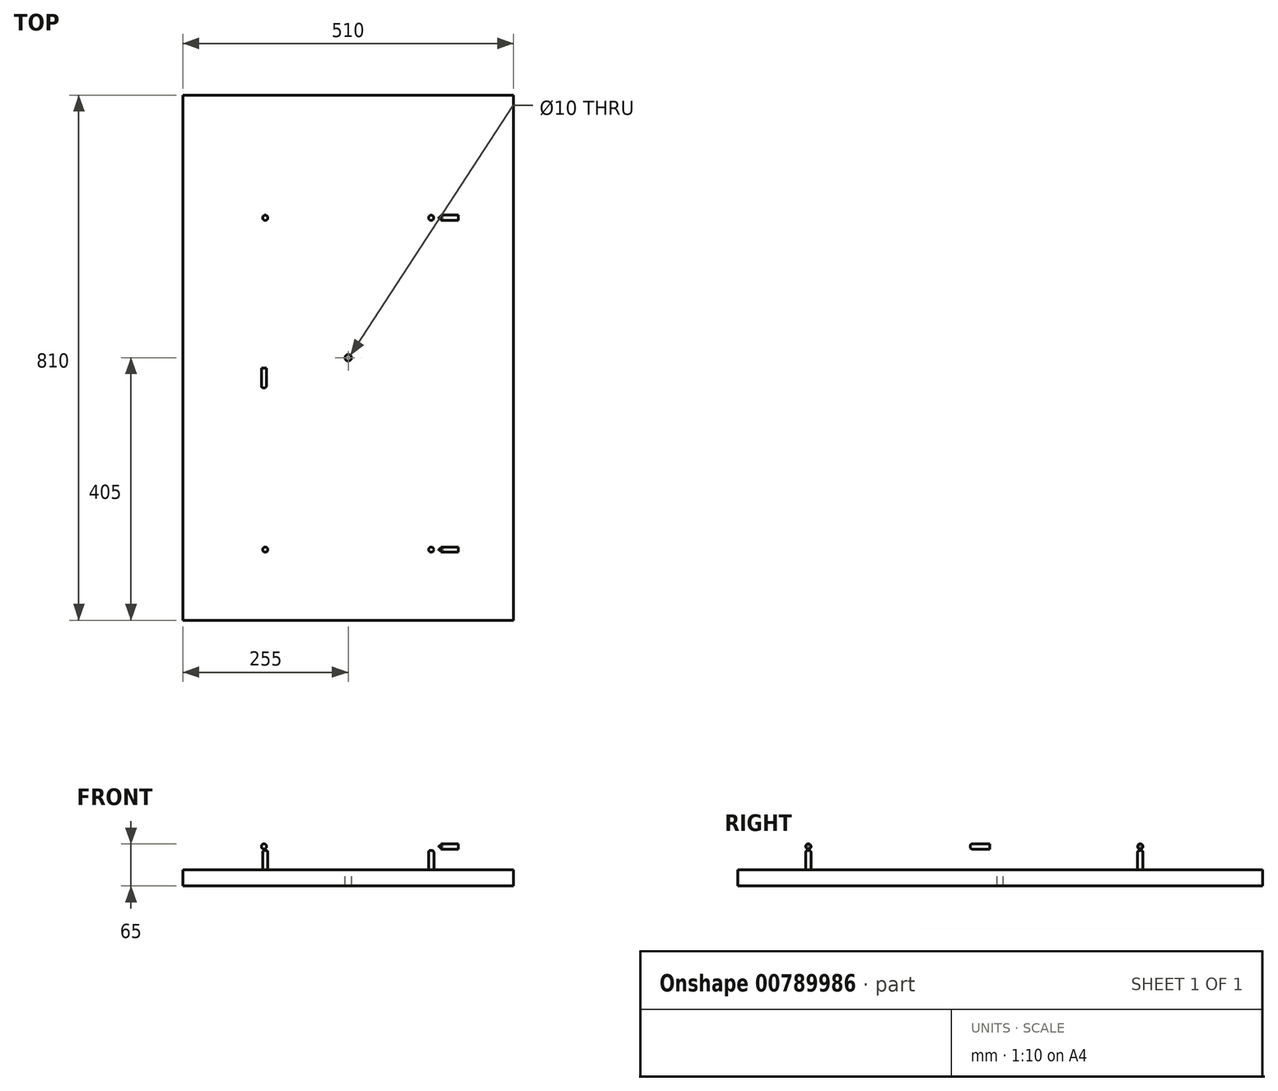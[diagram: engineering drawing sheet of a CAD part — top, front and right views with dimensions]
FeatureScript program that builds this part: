
annotation { "Feature Type Name" : "Feature", "Feature Type Description" : "" }
export const myFeature = defineFeature(function(context is Context, id is Id, definition is map)
    precondition{}
    {
        {
            var Q0;
            Q0=qCreatedBy(makeId("Right.planeOp"),FACE);
            var sketch = newSketch(context, id + "F0", { "sketchPlane" : qUnion([Q0])});
            skLineSegment(sketch, "E0.bottom", {"start": v(0, 0) * mm, "end": v(-810, 0) * mm});
            skLineSegment(sketch, "E0.top", {"start": v(0, 25) * mm, "end": v(-810, 25) * mm});
            skLineSegment(sketch, "E0.left", {"start": v(0, 0) * mm, "end": v(0, 25) * mm});
            skLineSegment(sketch, "E0.right", {"start": v(-810, 0) * mm, "end": v(-810, 25) * mm});
            skSolve(sketch);
        }
        {
            var Q0;
            Q0=makeQuery(id+"F0.imprint","IMPRINT",FACE,{"disambiguationData":[TD([[makeQuery(id+"F0.imprint","IMPRINT",EDGE,{"derivedFrom":sQuery(id+"F0.wireOp",EDGE,"E0.bottom")}),-1.0]])]});
            extrude(context, id + "F1", {"entities" : qUnion([Q0]), "depth" : 510 * mm, "offsetDistance" : 25 * mm});
        }
        {
            var Q0;
            Q0=makeQuery(id+"F1.opExtrude","SWEPT_FACE",FACE,{"disambiguationData":[OSD([sQuery(id+"F0.wireOp",EDGE,"E0.top")])]});
            var sketch = newSketch(context, id + "F2", { "sketchPlane" : qUnion([Q0])});
            skPoint(sketch, "E1", {"position": v(255, -405) * mm});
            skSolve(sketch);
        }
        {
            var Q0;
            Q0=sQuery(id+"F2.wireOp",VERTEX,"E1");
            var Q1;
            Q1=makeQuery(id+"F1.opExtrude","SWEPT_BODY",BODY,{"disambiguationData":[OSD([sQuery(id+"F0.wireOp",EDGE,"E0.bottom"),sQuery(id+"F0.wireOp",EDGE,"E0.top"),sQuery(id+"F0.wireOp",EDGE,"E0.left"),sQuery(id+"F0.wireOp",EDGE,"E0.right")])]});
            hole(context, id + "F3", {"style" : HoleStyle.SIMPLE, "endStyle" : HoleEndStyle.THROUGH, "holeDiameter" : 10 * mm, "majorDiameter" : 5 * mm, "isTappedThrough" : true, "tappedDepth" : 12 * mm, "tapClearance" : 3, "locations" : qUnion([Q0]), "scope" : qUnion([Q1])});
        }
        {
            var Q0;
            Q0=makeQuery(id+"F1.opExtrude","SWEPT_FACE",FACE,{"disambiguationData":[OSD([sQuery(id+"F0.wireOp",EDGE,"E0.top")])]});
            var sketch = newSketch(context, id + "F4", { "sketchPlane" : qUnion([Q0])});
            skLineSegment(sketch, "E2", {"start": v(255, -405) * mm, "end": v(127, -405) * mm});
            skLineSegment(sketch, "E3", {"start": v(127, -405) * mm, "end": v(127, -189) * mm});
            skCircle(sketch, "E4", {"center": v(127, -189) * mm, "radius": 4 * mm});
            skLineSegment(sketch, "E5", {"start": v(255, -405) * mm, "end": v(383, -405) * mm});
            skLineSegment(sketch, "E6", {"start": v(383, -405) * mm, "end": v(383, -189) * mm});
            skCircle(sketch, "E7", {"center": v(383, -189) * mm, "radius": 4 * mm});
            skLineSegment(sketch, "E8", {"start": v(127, -405) * mm, "end": v(127, -701) * mm});
            skLineSegment(sketch, "E9", {"start": v(383, -405) * mm, "end": v(383, -701) * mm});
            skCircle(sketch, "E10", {"center": v(127, -701) * mm, "radius": 4 * mm});
            skCircle(sketch, "E11", {"center": v(383, -701) * mm, "radius": 4 * mm});
            skSolve(sketch);
        }
        {
            var Q0;
            Q0=makeQuery(id+"F4.imprint","IMPRINT",FACE,{"disambiguationData":[TD([[makeQuery(id+"F4.imprint","IMPRINT",EDGE,{"derivedFrom":sQuery(id+"F4.wireOp",EDGE,"E10")}),1.0]])]});
            var Q1;
            Q1=makeQuery(id+"F4.imprint","IMPRINT",FACE,{"disambiguationData":[TD([[makeQuery(id+"F4.imprint","IMPRINT",EDGE,{"derivedFrom":sQuery(id+"F4.wireOp",EDGE,"E11")}),1.0]])]});
            var Q2;
            Q2=makeQuery(id+"F4.imprint","IMPRINT",FACE,{"disambiguationData":[TD([[makeQuery(id+"F4.imprint","IMPRINT",EDGE,{"derivedFrom":sQuery(id+"F4.wireOp",EDGE,"E7")}),1.0]])]});
            var Q3;
            Q3=makeQuery(id+"F4.imprint","IMPRINT",FACE,{"disambiguationData":[TD([[makeQuery(id+"F4.imprint","IMPRINT",EDGE,{"derivedFrom":sQuery(id+"F4.wireOp",EDGE,"E4")}),1.0]])]});
            extrude(context, id + "F5", {"entities" : qUnion([Q0, Q1, Q2, Q3]), "operationType" : NewBodyOperationType.ADD, "depth" : 30 * mm, "offsetDistance" : 25 * mm});
        }
        {
            var Q0;
            Q0=makeQuery(id+"F5.opExtrude","CAP_EDGE",EDGE,{"disambiguationData":[OSD([sQuery(id+"F4.wireOp",EDGE,"E10")])],"isStart":false});
            var Q1;
            Q1=makeQuery(id+"F5.opExtrude","CAP_FACE",FACE,{"disambiguationData":[OSD([sQuery(id+"F4.wireOp",EDGE,"E11")])],"isStart":false});
            var Q2;
            Q2=makeQuery(id+"F5.opExtrude","CAP_EDGE",EDGE,{"disambiguationData":[OSD([sQuery(id+"F4.wireOp",EDGE,"E7")])],"isStart":false});
            var Q3;
            Q3=makeQuery(id+"F5.opExtrude","CAP_EDGE",EDGE,{"disambiguationData":[OSD([sQuery(id+"F4.wireOp",EDGE,"E4")])],"isStart":false});
            fillet(context, id + "F6", {"entities" : qUnion([Q0, Q1, Q2, Q3]), "radius" : 3 * mm, "tangentPropagation" : true, "allowEdgeOverflow" : false});
        }
        {
            var Q0;
            Q0=qCreatedBy(makeId("Right.planeOp"),FACE);
            cPlane(context, id + "F7", {"entities" : qUnion([Q0]), "cplaneType" : CPlaneType.OFFSET, "offset" : 395 * mm, "width" : 150 * mm, "height" : 150 * mm});
        }
        {
            var Q0;
            Q0=qCreatedBy(makeId("Front.planeOp"),FACE);
            cPlane(context, id + "F8", {"entities" : qUnion([Q0]), "cplaneType" : CPlaneType.OFFSET, "offset" : 451.24 * mm, "width" : 150 * mm, "height" : 150 * mm});
        }
        {
            var Q0;
            Q0=qCreatedBy(id+"F7.planeOp",FACE);
            var sketch = newSketch(context, id + "F9", { "sketchPlane" : qUnion([Q0])});
            skLineSegment(sketch, "E12", {"start": v(0, 0) * mm, "end": v(0, 61) * mm});
            skLineSegment(sketch, "E13", {"start": v(0, 61) * mm, "end": v(-189, 61) * mm});
            skCircle(sketch, "E14", {"center": v(-189, 61) * mm, "radius": 4 * mm});
            skLineSegment(sketch, "E15", {"start": v(-189, 61) * mm, "end": v(-701, 61) * mm});
            skCircle(sketch, "E16", {"center": v(-701, 61) * mm, "radius": 4 * mm});
            skSolve(sketch);
        }
        {
            var Q0;
            Q0=makeQuery(id+"F9.imprint","IMPRINT",FACE,{"disambiguationData":[TD([[makeQuery(id+"F9.imprint","IMPRINT",EDGE,{"derivedFrom":sQuery(id+"F9.wireOp",EDGE,"E16")}),1.0]])]});
            var Q1;
            {var subQ0=sQuery(id+"F9.wireOp",EDGE,"E15");var subQ1=sQuery(id+"F9.wireOp",EDGE,"E13");var subQ2=makeQuery(id+"F9.imprint","INTERSECT",VERTEX,{"derivedFrom":[subQ1,subQ0]});Q1=makeQuery(id+"F9.imprint","IMPRINT",FACE,{"disambiguationData":[TD([[makeQuery(id+"F9.imprint","IMPRINT",EDGE,{"disambiguationData":[TD([[subQ2,1.0]])],"derivedFrom":subQ1}),-1.0]])]});}
            var Q2;
            {var subQ0=sQuery(id+"F9.wireOp",EDGE,"E15");var subQ1=sQuery(id+"F9.wireOp",EDGE,"E13");var subQ2=makeQuery(id+"F9.imprint","INTERSECT",VERTEX,{"derivedFrom":[subQ1,subQ0]});Q2=makeQuery(id+"F9.imprint","IMPRINT",FACE,{"disambiguationData":[TD([[makeQuery(id+"F9.imprint","IMPRINT",EDGE,{"disambiguationData":[TD([[subQ2,1.0]])],"derivedFrom":subQ1}),1.0]])]});}
            extrude(context, id + "F10", {"entities" : qUnion([Q0, Q1, Q2]), "depth" : 30 * mm, "offsetDistance" : 25 * mm});
        }
        {
            var Q0;
            Q0=makeQuery(id+"F10.opExtrude","CAP_EDGE",EDGE,{"disambiguationData":[OSD([sQuery(id+"F9.wireOp",EDGE,"E14")])],"isStart":true});
            var Q1;
            Q1=makeQuery(id+"F10.opExtrude","CAP_EDGE",EDGE,{"disambiguationData":[OSD([sQuery(id+"F9.wireOp",EDGE,"E16")])],"isStart":true});
            fillet(context, id + "F11", {"entities" : qUnion([Q0, Q1]), "radius" : 3 * mm, "tangentPropagation" : true, "allowEdgeOverflow" : false});
        }
        {
            var Q0;
            Q0=qCreatedBy(id+"F8.planeOp",FACE);
            var sketch = newSketch(context, id + "F12", { "sketchPlane" : qUnion([Q0])});
            skLineSegment(sketch, "E17", {"start": v(0, 0) * mm, "end": v(0, 61) * mm});
            skLineSegment(sketch, "E18", {"start": v(0, 61) * mm, "end": v(125, 61) * mm});
            skCircle(sketch, "E19", {"center": v(125, 61) * mm, "radius": 4 * mm});
            skSolve(sketch);
        }
        {
            var Q0;
            Q0=makeQuery(id+"F12.imprint","IMPRINT",FACE,{"disambiguationData":[TD([[makeQuery(id+"F12.imprint","IMPRINT",EDGE,{"derivedFrom":sQuery(id+"F12.wireOp",EDGE,"E19")}),1.0]])]});
            var Q1;
            Q1=sQuery(id+"F12.wireOp",EDGE,"E19");
            extrude(context, id + "F13", {"entities" : qUnion([Q0]), "surfaceEntities" : qUnion([Q1]), "oppositeDirection" : true, "depth" : 30 * mm, "offsetDistance" : 25 * mm});
        }
        {
            var Q0;
            Q0=makeQuery(id+"F13.opExtrude","CAP_EDGE",EDGE,{"disambiguationData":[OSD([sQuery(id+"F12.wireOp",EDGE,"E19")])],"isStart":true});
            fillet(context, id + "F14", {"entities" : qUnion([Q0]), "radius" : 3 * mm, "tangentPropagation" : true, "allowEdgeOverflow" : false});
        }
        {
            var Q0;
            Q0=qCreatedBy(makeId("Top.planeOp"),FACE);
            cPlane(context, id + "F15", {"entities" : qUnion([Q0]), "cplaneType" : CPlaneType.OFFSET, "offset" : 55 * mm, "width" : 150 * mm, "height" : 150 * mm});
        }
    });
